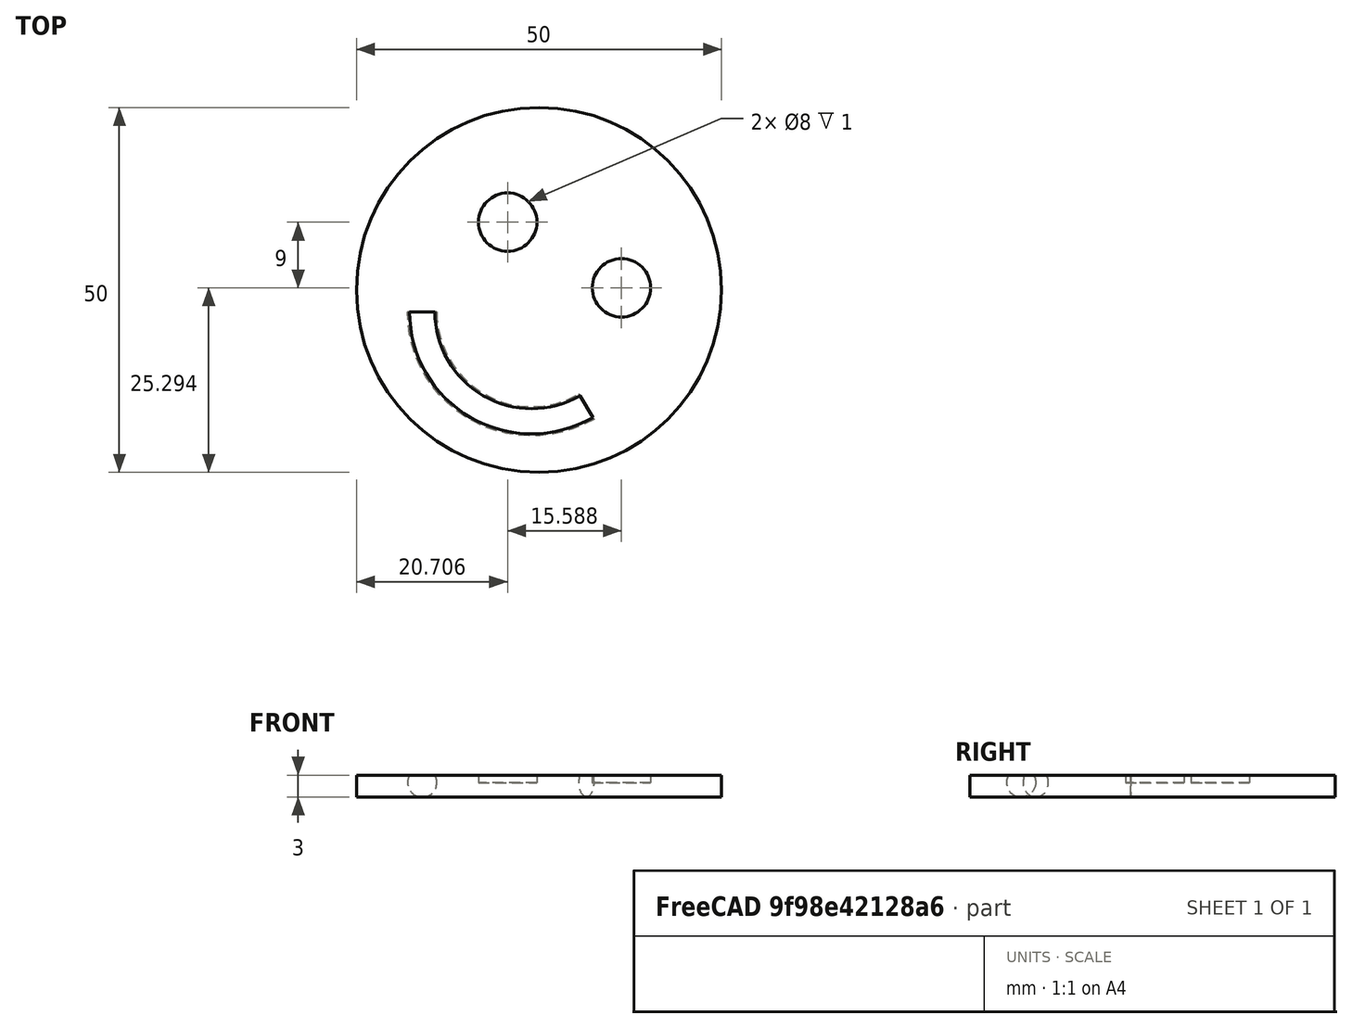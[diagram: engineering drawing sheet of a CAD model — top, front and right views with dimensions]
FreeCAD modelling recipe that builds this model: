
FCSTD DOCUMENT  (FreeCAD 0.21R33694 (Git))
Label: OJT1_T015R014_smile
License: All rights reserved
LicenseURL: http://en.wikipedia.org/wiki/All_rights_reserved
objects: Part::Cylinder×3, Part::Cut×2, Part::Torus×1, Part::MultiFuse×1
note: 7 computed .brp shape members not serialized (recipe doc carries the construction recipe); baked Part::Feature solids carry a one-line shape summary decoded from their .brp

FEATURE [Part::Cylinder] Cylinder  label="cara"
  Angle = 360
  AttacherType = Attacher::AttachEngine3D
  FirstAngle = 0
  Height = 3
  Radius = 25
  SecondAngle = 0
FEATURE [Part::Cylinder] Cylinder001  label="ull1"
  Angle = 360
  AttacherType = Attacher::AttachEngine3D
  FirstAngle = 0
  Height = 2
  Placement = pos=(9,9,2) rot=(0,0,1;0rad)
  Radius = 4
  SecondAngle = 0
FEATURE [Part::Cylinder] Cylinder002  label="ull2"
  Angle = 360
  AttacherType = Attacher::AttachEngine3D
  FirstAngle = 0
  Height = 2
  Placement = pos=(-9,9,2) rot=(0,0,1;0rad)
  Radius = 4
  SecondAngle = 0
FEATURE [Part::Torus] Torus
  Angle1 = -180
  Angle2 = 180
  Angle3 = 120
  AttacherType = Attacher::AttachEngine3D
  Placement = pos=(-1,-3,2) rot=(0,0,1;3.14159rad)
  Radius1 = 15
  Radius2 = 2
FEATURE [Part::MultiFuse] Fusion
  Placement = pos=(-1,-3,0) rot=(0,0,-1;0.523599rad)
  Refine = true
  Shapes = -> [Cylinder002,Cylinder001]
FEATURE [Part::Cut] Cut
  Base = -> Cylinder
  Refine = true
  Tool = -> Torus
FEATURE [Part::Cut] Cut001
  Base = -> Cut
  Refine = true
  Tool = -> Fusion
